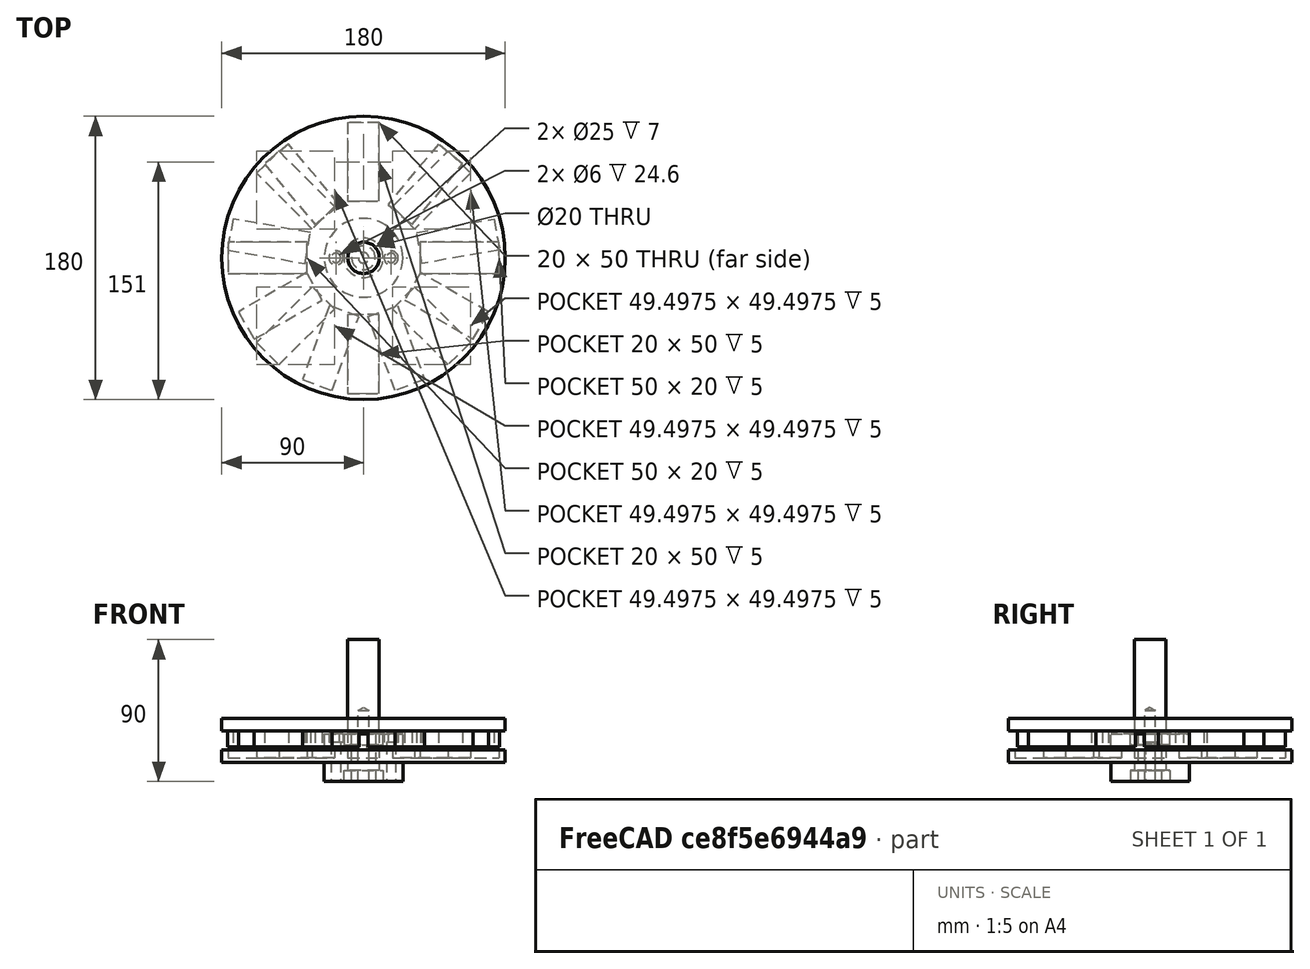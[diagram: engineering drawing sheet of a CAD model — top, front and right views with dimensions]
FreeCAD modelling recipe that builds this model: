
FCSTD DOCUMENT  (FreeCAD 0.20R29410 (Git))
Label: windTurbine
License: All rights reserved
LicenseURL: http://en.wikipedia.org/wiki/All_rights_reserved
objects: Sketcher::SketchObject×18, PartDesign::Pocket×10, PartDesign::Pad×6, TechDraw::DrawViewDimension×4, PartDesign::Hole×3, PartDesign::Body×3, PartDesign::Plane×1, TechDraw::DrawSVGTemplate×1, TechDraw::DrawViewPart×1, TechDraw::DrawViewSection×1, TechDraw::DrawViewSymbol×1, TechDraw::DrawPage×1
note: 60 computed .brp shape members not serialized (recipe doc carries the construction recipe); baked Part::Feature solids carry a one-line shape summary decoded from their .brp

FEATURE [Sketcher::SketchObject] Sketch  label="RotorDisc"
  FullyConstrained = true
  sketch-geometry (1):
    g0: Circle CenterX=0 CenterY=0 CenterZ=0 NormalX=0 NormalY=0 NormalZ=1 AngleXU=0 Radius=90
  constraints (2):
    c: Coincident(g0,g-1)
    c: Diameter(g0) = 180
FEATURE [Sketcher::SketchObject] Sketch001  label="Mag1"
  FullyConstrained = true
  MapMode = 5
  Support = -> [XY_Plane001]
  sketch-geometry (4):
    g0: LineSegment StartX=-10 StartY=86 StartZ=0 EndX=10 EndY=86 EndZ=0
    g1: LineSegment StartX=10 StartY=86 StartZ=0 EndX=10 EndY=36 EndZ=0
    g2: LineSegment StartX=10 StartY=36 StartZ=0 EndX=-10 EndY=36 EndZ=0
    g3: LineSegment StartX=-10 StartY=36 StartZ=0 EndX=-10 EndY=86 EndZ=0
  constraints (11):
    c: Coincident(g0,g1)
    c: Coincident(g1,g2)
    c: Coincident(g2,g3)
    c: Coincident(g3,g0)
    c: Horizontal(g2)
    c: Vertical(g1)
    c: Vertical(g3)
    c: Symmetric(g0,g0,g-2)
    c: DistanceY(g1,g1) = 50
    c: DistanceY(g-1,g1) = 36
    c: DistanceX(g0,g0) = 20
FEATURE [Sketcher::SketchObject] Sketch002  label="Mag2"
  FullyConstrained = true
  MapMode = 5
  Support = -> [XY_Plane001]
  sketch-geometry (4):
    g0: LineSegment StartX=-10 StartY=-36 StartZ=0 EndX=10 EndY=-36 EndZ=0
    g1: LineSegment StartX=10 StartY=-36 StartZ=0 EndX=10 EndY=-86 EndZ=0
    g2: LineSegment StartX=10 StartY=-86 StartZ=0 EndX=-10 EndY=-86 EndZ=0
    g3: LineSegment StartX=-10 StartY=-86 StartZ=0 EndX=-10 EndY=-36 EndZ=0
  constraints (12):
    c: Coincident(g0,g1)
    c: Coincident(g1,g2)
    c: Coincident(g2,g3)
    c: Coincident(g3,g0)
    c: Horizontal(g2)
    c: DistanceX(g0,g0) = 20
    c: DistanceY(g1,g0) = 50
    c: Angle(g3,g2,g2) = 1.5708
    c: Angle(g2,g1,g1) = 1.5708
    c: Angle(g0,g3,g0) = 1.5708
    c: DistanceX(g-1,g0) = 10
    c: DistanceY(g0,g-1) = 36
FEATURE [Sketcher::SketchObject] Sketch003  label="Mag3"
  FullyConstrained = true
  MapMode = 5
  Support = -> [XY_Plane001]
  sketch-geometry (4):
    g0: LineSegment StartX=36 StartY=10 StartZ=0 EndX=86 EndY=10 EndZ=0
    g1: LineSegment StartX=86 StartY=10 StartZ=0 EndX=86 EndY=-10 EndZ=0
    g2: LineSegment StartX=86 StartY=-10 StartZ=0 EndX=36 EndY=-10 EndZ=0
    g3: LineSegment StartX=36 StartY=-10 StartZ=0 EndX=36 EndY=10 EndZ=0
  constraints (11):
    c: Coincident(g0,g1)
    c: Coincident(g1,g2)
    c: Coincident(g2,g3)
    c: Coincident(g3,g0)
    c: Horizontal(g0)
    c: Horizontal(g2)
    c: Vertical(g1)
    c: DistanceX(g0,g0) = 50
    c: Symmetric(g2,g0,g-1)
    c: DistanceY(g3,g3) = 20
    c: DistanceX(g-1,g2) = 36
FEATURE [Sketcher::SketchObject] Sketch004  label="Mag4"
  FullyConstrained = true
  MapMode = 5
  Support = -> [XY_Plane001]
  sketch-geometry (4):
    g0: LineSegment StartX=-86 StartY=10 StartZ=0 EndX=-36 EndY=10 EndZ=0
    g1: LineSegment StartX=-36 StartY=10 StartZ=0 EndX=-36 EndY=-10 EndZ=0
    g2: LineSegment StartX=-36 StartY=-10 StartZ=0 EndX=-86 EndY=-10 EndZ=0
    g3: LineSegment StartX=-86 StartY=-10 StartZ=0 EndX=-86 EndY=10 EndZ=0
  constraints (12):
    c: Coincident(g0,g1)
    c: Coincident(g1,g2)
    c: Coincident(g2,g3)
    c: Coincident(g3,g0)
    c: DistanceY(g1,g0) = 20
    c: DistanceX(g0,g0) = 50
    c: Equal(g0,g2)
    c: Equal(g3,g1)
    c: Perpendicular(g3,g0)
    c: DistanceX(g0,g-1) = 36
    c: Perpendicular(g-2,g2)
    c: DistanceY(g-1,g0) = 10
FEATURE [Sketcher::SketchObject] Sketch005  label="Mag5"
  FullyConstrained = true
  MapMode = 5
  Support = -> [XY_Plane001]
  sketch-geometry (5):
    g0: LineSegment StartX=-63.6215 StartY=63.6215 StartZ=0 EndX=0 EndY=0 EndZ=0
    g1: LineSegment StartX=-67.8823 StartY=53.7401 StartZ=0 EndX=-32.5269 EndY=18.3848 EndZ=0
    g2: LineSegment StartX=-32.5269 StartY=18.3848 StartZ=0 EndX=-18.3848 EndY=32.5269 EndZ=0
    g3: LineSegment StartX=-18.3848 StartY=32.5269 StartZ=0 EndX=-53.7401 EndY=67.8823 EndZ=0
    g4: LineSegment StartX=-53.7401 StartY=67.8823 StartZ=0 EndX=-67.8823 EndY=53.7401 EndZ=0
  constraints (15):
    c: Coincident(g0,g-1)
    c: DistanceX(g0) = -63.6215
    c: Coincident(g1,g2)
    c: Coincident(g2,g3)
    c: Coincident(g3,g4)
    c: Coincident(g4,g1)
    c: Distance(g3,g0) = 10
    c: Distance(g2,g0) = 10
    c: Distance(g1,g0) = 10
    c: Distance(g1,g0) = 10
    c: Distance(g2,g3) = 50
    c: Distance(g1,g1) = 50
    c: Perpendicular(g1,g4)
    c: Distance(g0,g2) = 36
    c: Angle(g-1,g0) = 2.35619
FEATURE [Sketcher::SketchObject] Sketch006  label="Mag6"
  FullyConstrained = true
  MapMode = 5
  Support = -> [XY_Plane001]
  sketch-geometry (5):
    g0: LineSegment StartX=0 StartY=0 StartZ=0 EndX=70.7107 EndY=70.7107 EndZ=0
    g1: LineSegment StartX=18.3848 StartY=32.5269 StartZ=0 EndX=32.5269 EndY=18.3848 EndZ=0
    g2: LineSegment StartX=32.5269 StartY=18.3848 StartZ=0 EndX=67.8823 EndY=53.7401 EndZ=0
    g3: LineSegment StartX=67.8823 StartY=53.7401 StartZ=0 EndX=53.7401 EndY=67.8823 EndZ=0
    g4: LineSegment StartX=53.7401 StartY=67.8823 StartZ=0 EndX=18.3848 EndY=32.5269 EndZ=0
  constraints (15):
    c: Coincident(g0,g-1)
    c: Angle(g-1,g0) = 0.785398
    c: Coincident(g1,g2)
    c: Coincident(g2,g3)
    c: Coincident(g3,g4)
    c: Coincident(g4,g1)
    c: Distance(g1,g1) = 20
    c: Distance(g3,g2) = 20
    c: Distance(g2,g1) = 50
    c: Distance(g1,g3) = 50
    c: Distance(g0,g1) = 36
    c: Parallel(g4,g0)
    c: Perpendicular(g3,g4)
    c: Distance(g1,g0) = 10
    c: Distance(g0) = 100
FEATURE [Sketcher::SketchObject] Sketch007  label="Mag7"
  FullyConstrained = true
  MapMode = 5
  Support = -> [XY_Plane001]
  sketch-geometry (5):
    g0: LineSegment StartX=0 StartY=0 StartZ=0 EndX=-93.0623 EndY=-93.0623 EndZ=0
    g1: LineSegment StartX=-67.8823 StartY=-53.7401 StartZ=0 EndX=-53.7401 EndY=-67.8823 EndZ=0
    g2: LineSegment StartX=-53.7401 StartY=-67.8823 StartZ=0 EndX=-18.3848 EndY=-32.5269 EndZ=0
    g3: LineSegment StartX=-18.3848 StartY=-32.5269 StartZ=0 EndX=-32.5269 EndY=-18.3848 EndZ=0
    g4: LineSegment StartX=-32.5269 StartY=-18.3848 StartZ=0 EndX=-67.8823 EndY=-53.7401 EndZ=0
  constraints (15):
    c: Coincident(g0,g-1)
    c: Angle(g0,g-1) = 2.35619
    c: Distance(g0) = 131.61
    c: Coincident(g1,g2)
    c: Coincident(g2,g3)
    c: Coincident(g3,g4)
    c: Coincident(g4,g1)
    c: Distance(g4) = 50
    c: Distance(g2) = 50
    c: Distance(g3) = 20
    c: Distance(g1) = 20
    c: Perpendicular(g4,g1)
    c: Distance(g3,g0) = 10
    c: Distance(g0,g3) = 36
    c: Parallel(g0,g4)
FEATURE [Sketcher::SketchObject] Sketch008  label="Mag8"
  FullyConstrained = true
  MapMode = 5
  Support = -> [XY_Plane001]
  sketch-geometry (5):
    g0: LineSegment StartX=0 StartY=0 StartZ=0 EndX=70.7107 EndY=-70.7107 EndZ=0
    g1: LineSegment StartX=18.3848 StartY=-32.5269 StartZ=0 EndX=32.5269 EndY=-18.3848 EndZ=0
    g2: LineSegment StartX=32.5269 StartY=-18.3848 StartZ=0 EndX=67.8823 EndY=-53.7401 EndZ=0
    g3: LineSegment StartX=67.8823 StartY=-53.7401 StartZ=0 EndX=53.7401 EndY=-67.8823 EndZ=0
    g4: LineSegment StartX=53.7401 StartY=-67.8823 StartZ=0 EndX=18.3848 EndY=-32.5269 EndZ=0
  constraints (15):
    c: Coincident(g0,g-1)
    c: Angle(g0,g-1) = 0.785398
    c: Distance(g0) = 100
    c: Coincident(g1,g2)
    c: Coincident(g2,g3)
    c: Coincident(g3,g4)
    c: Coincident(g4,g1)
    c: Parallel(g4,g0)
    c: Perpendicular(g2,g3)
    c: Distance(g1) = 20
    c: Distance(g3) = 20
    c: Distance(g2) = 50
    c: Distance(g4) = 50
    c: Distance(g1,g0) = 10
    c: Distance(g0,g1) = 36
FEATURE [Sketcher::SketchObject] Sketch009  label="BearingSeatAndBoss"
  FullyConstrained = true
  MapMode = 5
  Support = -> [XY_Plane001]
  sketch-geometry (4):
    g0: Circle CenterX=0 CenterY=0 CenterZ=0 NormalX=0 NormalY=0 NormalZ=1 AngleXU=0 Radius=25
    g1: Circle CenterX=0 CenterY=0 CenterZ=0 NormalX=0 NormalY=0 NormalZ=1 AngleXU=0 Radius=17.5
    g2: GeomPoint X=-17.5 Y=0 Z=0
    g3: GeomPoint X=17.5 Y=0 Z=0
  constraints (8):
    c: Coincident(g0,g-1)
    c: Diameter(g0) = 50
    c: Coincident(g1,g0)
    c: Diameter(g1) = 35
    c: PointOnObject(g2,g1)
    c: PointOnObject(g3,g1)
    c: DistanceY(g2) = 0
    c: DistanceY(g3) = 0
FEATURE [PartDesign::Pad] Pad
  Direction = (0,0,1)
  Length = 8
  Length2 = 10
  Profile = -> Sketch
  ReferenceAxis = -> Sketch [N_Axis]
  Refine = true
  Type = 0
FEATURE [PartDesign::Pocket] Pocket
  BaseFeature = -> Pad
  Direction = (0,0,-1)
  Length = 5
  Length2 = 5
  Profile = -> Sketch001
  ReferenceAxis = -> Sketch001 [N_Axis]
  Refine = true
  Reversed = true
  Type = 0
FEATURE [PartDesign::Pocket] Pocket001
  BaseFeature = -> Pocket
  Direction = (0,0,-1)
  Length = 5
  Length2 = 5
  Profile = -> Sketch002
  ReferenceAxis = -> Sketch002 [N_Axis]
  Refine = true
  Reversed = true
  Type = 0
FEATURE [PartDesign::Pocket] Pocket002
  BaseFeature = -> Pocket001
  Direction = (0,0,-1)
  Length = 5
  Length2 = 5
  Profile = -> Sketch003
  ReferenceAxis = -> Sketch003 [N_Axis]
  Refine = true
  Reversed = true
  Type = 0
FEATURE [PartDesign::Pocket] Pocket003
  BaseFeature = -> Pocket002
  Direction = (0,0,-1)
  Length = 5
  Length2 = 5
  Profile = -> Sketch004
  ReferenceAxis = -> Sketch004 [N_Axis]
  Refine = true
  Reversed = true
  Type = 0
FEATURE [PartDesign::Pocket] Pocket004
  BaseFeature = -> Pocket003
  Direction = (0,0,-1)
  Length = 5
  Length2 = 5
  Profile = -> Sketch005
  ReferenceAxis = -> Sketch005 [N_Axis]
  Refine = true
  Reversed = true
  Type = 0
FEATURE [PartDesign::Pocket] Pocket005
  BaseFeature = -> Pocket004
  Direction = (0,0,-1)
  Length = 5
  Length2 = 5
  Profile = -> Sketch006
  ReferenceAxis = -> Sketch006 [N_Axis]
  Refine = true
  Reversed = true
  Type = 0
FEATURE [PartDesign::Pocket] Pocket006
  BaseFeature = -> Pocket005
  Direction = (0,0,-1)
  Length = 5
  Length2 = 5
  Profile = -> Sketch007
  ReferenceAxis = -> Sketch007 [N_Axis]
  Refine = true
  Reversed = true
  Type = 0
FEATURE [PartDesign::Pocket] Pocket007
  BaseFeature = -> Pocket006
  Direction = (0,0,-1)
  Length = 5
  Length2 = 5
  Profile = -> Sketch008
  ReferenceAxis = -> Sketch008 [N_Axis]
  Refine = true
  Reversed = true
  Type = 0
FEATURE [PartDesign::Pad] Pad001
  BaseFeature = -> Pocket007
  Direction = (0,0,1)
  Length = 20
  Length2 = 10
  Profile = -> Sketch009
  ReferenceAxis = -> Sketch009 [N_Axis]
  Refine = true
  Type = 4
FEATURE [Sketcher::SketchObject] Sketch010
  FullyConstrained = true
  MapMode = 5
  Placement = pos=(0,0,-10) rot=(1,0,0;3.14159rad)
  Support = -> [Pad001]
  sketch-geometry (1):
    g0: Circle CenterX=0 CenterY=0 CenterZ=0 NormalX=0 NormalY=0 NormalZ=1 AngleXU=0 Radius=10
  constraints (2):
    c: Coincident(g0,g-1)
    c: Diameter(g0) = 20
FEATURE [PartDesign::Hole] Hole
  BaseFeature = -> Pad001
  CustomThreadClearance = 0
  Depth = 517.767
  DepthType = 1
  Diameter = 20
  DrillForDepth = false
  DrillPoint = 1
  DrillPointAngle = 118
  HoleCutCountersinkAngle = 90
  HoleCutCustomValues = false
  HoleCutDepth = 0
  HoleCutDiameter = 6.1
  HoleCutType = 0
  ModelThread = false
  Profile = -> Sketch010
  Refine = true
  Tapered = false
  TaperedAngle = 90
  ThreadClass = 0
  ThreadDepth = 517.767
  ThreadDepthType = 0
  ThreadDirection = 0
  ThreadFit = 0
  ThreadSize = 0
  ThreadType = 0
  Threaded = false
  UseCustomThreadClearance = false
FEATURE [Sketcher::SketchObject] Sketch011
  FullyConstrained = true
  MapMode = 5
  Placement = pos=(0,0,-10) rot=(1,0,0;3.14159rad)
  Support = -> [Hole]
  sketch-geometry (1):
    g0: Circle CenterX=0 CenterY=0 CenterZ=0 NormalX=0 NormalY=0 NormalZ=1 AngleXU=0 Radius=12.5
  constraints (2):
    c: Coincident(g0,g-1)
    c: Diameter(g0) = 25
FEATURE [PartDesign::Pocket] Pocket008
  BaseFeature = -> Hole
  Direction = (0,0,1)
  Length = 7
  Length2 = 5
  Profile = -> Sketch011
  ReferenceAxis = -> Sketch011 [N_Axis]
  Refine = true
  Type = 0
FEATURE [Sketcher::SketchObject] Sketch012
  FullyConstrained = true
  MapMode = 5
  Placement = pos=(0,0,20) rot=(0,0,1;0rad)
  Support = -> [Pocket008]
  sketch-geometry (1):
    g0: Circle CenterX=0 CenterY=0 CenterZ=0 NormalX=0 NormalY=0 NormalZ=1 AngleXU=0 Radius=12.5
  constraints (2):
    c: Coincident(g0,g-1)
    c: Diameter(g0) = 25
FEATURE [PartDesign::Pocket] Pocket009
  BaseFeature = -> Pocket008
  Direction = (0,0,-1)
  Length = 7
  Length2 = 5
  Profile = -> Sketch012
  ReferenceAxis = -> Sketch012 [N_Axis]
  Refine = true
  Type = 0
FEATURE [Sketcher::SketchObject] Sketch013
  FullyConstrained = true
  MapMode = 5
  Placement = pos=(0,0,-10) rot=(1,0,0;3.14159rad)
  Support = -> [Pocket009]
  sketch-geometry (5):
    g0: Circle CenterX=0 CenterY=0 CenterZ=0 NormalX=0 NormalY=0 NormalZ=1 AngleXU=0 Radius=17.5
    g1: GeomPoint X=-17.5 Y=0 Z=0
    g2: GeomPoint X=17.5 Y=0 Z=0
    g3: Circle CenterX=17.5 CenterY=0 CenterZ=0 NormalX=0 NormalY=0 NormalZ=1 AngleXU=0 Radius=3
    g4: Circle CenterX=-17.5 CenterY=0 CenterZ=0 NormalX=0 NormalY=0 NormalZ=1 AngleXU=0 Radius=3
  constraints (10):
    c: Coincident(g0,g-1)
    c: PointOnObject(g1,g0)
    c: PointOnObject(g2,g0)
    c: Diameter(g0) = 35
    c: DistanceY(g1) = 0
    c: DistanceY(g2) = 0
    c: Coincident(g3,g2)
    c: Coincident(g4,g1)
    c: Diameter(g3) = 6
    c: Diameter(g4) = 6
FEATURE [PartDesign::Hole] Hole001
  BaseFeature = -> Pocket009
  CustomThreadClearance = 0
  Depth = 517.767
  DepthType = 1
  Diameter = 6
  DrillForDepth = false
  DrillPoint = 1
  DrillPointAngle = 118
  HoleCutCountersinkAngle = 90
  HoleCutCustomValues = false
  HoleCutDepth = 5.4
  HoleCutDiameter = 9
  HoleCutType = 1
  ModelThread = false
  Profile = -> Sketch013
  Refine = true
  Tapered = false
  TaperedAngle = 90
  ThreadClass = 0
  ThreadDepth = 517.767
  ThreadDepthType = 0
  ThreadDirection = 0
  ThreadFit = 0
  ThreadSize = 0
  ThreadType = 0
  Threaded = false
  UseCustomThreadClearance = false
FEATURE [PartDesign::Body] Body  label="RotorBody"
  Group = -> [Sketch,Sketch001,Sketch002,Sketch003,Sketch004,Sketch005,Sketch006,Sketch007,Sketch008,Sketch009,Pad,Pocket,Pocket001,Pocket002,Pocket003,Pocket004,Pocket005,Pocket006,Pocket007,Pad001,Sketch010,Hole,Sketch011,Pocket008,Sketch012,Pocket009,Sketch013,Hole001]
  Origin = -> Origin001
  Placement = pos=(-1e-15,0,10) rot=(0,1,0;3.14159rad)
  Tip = -> Hole001
FEATURE [Sketcher::SketchObject] Sketch014
  FullyConstrained = true
  MapMode = 5
  Placement = pos=(0,0,20) rot=(0,0,1;0rad)
  sketch-geometry (1):
    g0: Circle CenterX=0 CenterY=0 CenterZ=0 NormalX=0 NormalY=0 NormalZ=1 AngleXU=0 Radius=10
  constraints (2):
    c: Coincident(g0,g-1)
    c: Diameter(g0) = 20
FEATURE [PartDesign::Pad] Pad002
  Direction = (0,0,1)
  Length = 60
  Length2 = 10
  Placement = pos=(0,0,20) rot=(0,0,1;0rad)
  Profile = -> Sketch014
  ReferenceAxis = -> Sketch014 [N_Axis]
  Refine = true
  Type = 0
FEATURE [Sketcher::SketchObject] Sketch015
  FullyConstrained = true
  MapMode = 5
  Placement = pos=(0,0,20) rot=(1,0,0;3.14159rad)
  Support = -> [Pad002]
  sketch-geometry (1):
    g0: Circle CenterX=0 CenterY=0 CenterZ=0 NormalX=0 NormalY=0 NormalZ=1 AngleXU=0 Radius=7.5
  constraints (2):
    c: Coincident(g0,g-1)
    c: Diameter(g0) = 15
FEATURE [PartDesign::Pad] Pad003
  BaseFeature = -> Pad002
  Direction = (0,0,-1)
  Length = 30
  Length2 = 10
  Placement = pos=(0,0,20) rot=(0,0,1;0rad)
  Profile = -> Sketch015
  ReferenceAxis = -> Sketch015 [N_Axis]
  Refine = true
  Type = 0
FEATURE [PartDesign::Hole] Hole002
  BaseFeature = -> Pad003
  CustomThreadClearance = 0
  Depth = 45
  DepthType = 0
  Diameter = 6.8
  DrillForDepth = false
  DrillPoint = 1
  DrillPointAngle = 118
  HoleCutCountersinkAngle = 90
  HoleCutCustomValues = false
  HoleCutDepth = 0
  HoleCutDiameter = 6.1
  HoleCutType = 0
  ModelThread = false
  Placement = pos=(0,0,20) rot=(0,0,1;0rad)
  Profile = -> Pad003 [Face5]
  Refine = true
  Tapered = false
  TaperedAngle = 90
  ThreadClass = 0
  ThreadDepth = 45
  ThreadDepthType = 0
  ThreadDirection = 0
  ThreadFit = 0
  ThreadSize = 16
  ThreadType = 1
  Threaded = true
  UseCustomThreadClearance = false
FEATURE [PartDesign::Body] Body001  label="Shaft"
  Group = -> [Sketch014,Pad002,Sketch015,Pad003,Hole002]
  Origin = -> Origin
  Tip = -> Hole002
FEATURE [PartDesign::Plane] DatumPlane
  AttachmentOffset = pos=(0,0,21) rot=(0,0,1;0rad)
  Length = 216
  MapMode = 5
  Placement = pos=(0,0,21) rot=(0,0,1;0rad)
  ResizeMode = 0
  Support = -> [XY_Plane001]
  Width = 216
FEATURE [Sketcher::SketchObject] Sketch016
  FullyConstrained = true
  MapMode = 5
  Placement = pos=(0,0,21) rot=(0,0,1;0rad)
  Support = -> [DatumPlane]
  sketch-geometry (2):
    g0: Circle CenterX=0 CenterY=0 CenterZ=0 NormalX=0 NormalY=0 NormalZ=1 AngleXU=0 Radius=90
    g1: Circle CenterX=0 CenterY=0 CenterZ=0 NormalX=0 NormalY=0 NormalZ=1 AngleXU=0 Radius=10
  constraints (4):
    c: Coincident(g0,g-1)
    c: Diameter(g0) = 180
    c: Coincident(g1,g0)
    c: Diameter(g1) = 20
FEATURE [PartDesign::Pad] Pad004
  Direction = (0,0,1)
  Length = 8
  Length2 = 10
  Placement = pos=(0,0,21) rot=(0,0,1;0rad)
  Profile = -> Sketch016
  ReferenceAxis = -> Sketch016 [N_Axis]
  Refine = true
  Type = 0
FEATURE [Sketcher::SketchObject] Sketch017
  FullyConstrained = true
  MapMode = 5
  Placement = pos=(0,0,21) rot=(0,0,1;0rad)
  Support = -> [DatumPlane]
  sketch-geometry (50):
    g0: LineSegment StartX=0 StartY=0 StartZ=0 EndX=0 EndY=10 EndZ=0
    g1: LineSegment StartX=0 StartY=0 StartZ=0 EndX=6.42788 EndY=7.66044 EndZ=0
    g2: LineSegment StartX=0 StartY=0 StartZ=0 EndX=9.84808 EndY=1.73648 EndZ=0
    g3: LineSegment StartX=0 StartY=0 StartZ=0 EndX=8.66025 EndY=-5 EndZ=0
    g4: LineSegment StartX=0 StartY=0 StartZ=0 EndX=3.4202 EndY=-9.39693 EndZ=0
    g5: LineSegment StartX=0 StartY=0 StartZ=0 EndX=-3.4202 EndY=-9.39693 EndZ=0
    g6: LineSegment StartX=0 StartY=0 StartZ=0 EndX=-8.66025 EndY=-5 EndZ=0
    g7: LineSegment StartX=0 StartY=0 StartZ=0 EndX=-9.84808 EndY=1.73648 EndZ=0
    g8: LineSegment StartX=0 StartY=0 StartZ=0 EndX=-6.42788 EndY=7.66044 EndZ=0
    g9: LineSegment StartX=-10 StartY=86 StartZ=0 EndX=-10 EndY=36 EndZ=0
    g10: LineSegment StartX=-10 StartY=36 StartZ=0 EndX=10 EndY=36 EndZ=0
    g11: LineSegment StartX=10 StartY=36 StartZ=0 EndX=10 EndY=86 EndZ=0
    g12: LineSegment StartX=10 StartY=86 StartZ=0 EndX=-10 EndY=86 EndZ=0
    g13: LineSegment StartX=15.4799 StartY=34.0055 StartZ=0 EndX=30.8008 EndY=21.1497 EndZ=0
    g14: LineSegment StartX=30.8008 StartY=21.1497 StartZ=0 EndX=62.9402 EndY=59.4519 EndZ=0
    g15: LineSegment StartX=62.9402 StartY=59.4519 StartZ=0 EndX=47.6193 EndY=72.3077 EndZ=0
    g16: LineSegment StartX=47.6193 StartY=72.3077 StartZ=0 EndX=15.4799 EndY=34.0055 EndZ=0
    g17: LineSegment StartX=37.1896 StartY=-3.59674 StartZ=0 EndX=33.7166 EndY=16.0994 EndZ=0
    g18: LineSegment StartX=33.7166 StartY=16.0994 StartZ=0 EndX=82.957 EndY=24.7818 EndZ=0
    g19: LineSegment StartX=82.957 StartY=24.7818 StartZ=0 EndX=86.4299 EndY=5.08567 EndZ=0
    g20: LineSegment StartX=86.4299 StartY=5.08567 StartZ=0 EndX=37.1896 EndY=-3.59674 EndZ=0
    g21: LineSegment StartX=36.1769 StartY=-9.33975 StartZ=0 EndX=26.1769 EndY=-26.6603 EndZ=0
    g22: LineSegment StartX=26.1769 StartY=-26.6603 StartZ=0 EndX=69.4782 EndY=-51.6603 EndZ=0
    g23: LineSegment StartX=69.4782 StartY=-51.6603 StartZ=0 EndX=79.4782 EndY=-34.3397 EndZ=0
    g24: LineSegment StartX=79.4782 StartY=-34.3397 StartZ=0 EndX=36.1769 EndY=-9.33975 EndZ=0
    g25: LineSegment StartX=2.9158 StartY=-37.2492 StartZ=0 EndX=21.7096 EndY=-30.4087 EndZ=0
    g26: LineSegment StartX=21.7096 StartY=-30.4087 StartZ=0 EndX=38.8107 EndY=-77.3933 EndZ=0
    g27: LineSegment StartX=38.8107 StartY=-77.3933 StartZ=0 EndX=20.0168 EndY=-84.2338 EndZ=0
    g28: LineSegment StartX=20.0168 StartY=-84.2338 StartZ=0 EndX=2.9158 EndY=-37.2492 EndZ=0
    g29: LineSegment StartX=-20.0168 StartY=-84.2338 StartZ=0 EndX=-2.9158 EndY=-37.2491 EndZ=0
    g30: LineSegment StartX=-2.9158 StartY=-37.2491 StartZ=0 EndX=-21.7097 EndY=-30.4087 EndZ=0
    g31: LineSegment StartX=-21.7097 StartY=-30.4087 StartZ=0 EndX=-38.8107 EndY=-77.3934 EndZ=0
    g32: LineSegment StartX=-38.8107 StartY=-77.3934 StartZ=0 EndX=-20.0168 EndY=-84.2338 EndZ=0
    g33: LineSegment StartX=-79.4782 StartY=-34.3397 StartZ=0 EndX=-69.4782 EndY=-51.6603 EndZ=0
    g34: LineSegment StartX=-69.4782 StartY=-51.6603 StartZ=0 EndX=-26.1769 EndY=-26.6603 EndZ=0
    g35: LineSegment StartX=-26.1769 StartY=-26.6603 StartZ=0 EndX=-36.1769 EndY=-9.33975 EndZ=0
    g36: LineSegment StartX=-36.1769 StartY=-9.33975 StartZ=0 EndX=-79.4782 EndY=-34.3397 EndZ=0
    g37: LineSegment StartX=-82.957 StartY=24.7818 StartZ=0 EndX=-86.4299 EndY=5.08567 EndZ=0
    g38: LineSegment StartX=-86.4299 StartY=5.08567 StartZ=0 EndX=-37.1896 EndY=-3.59674 EndZ=0
    g39: LineSegment StartX=-37.1896 StartY=-3.59674 StartZ=0 EndX=-33.7166 EndY=16.0994 EndZ=0
    g40: LineSegment StartX=-33.7166 StartY=16.0994 StartZ=0 EndX=-82.957 EndY=24.7818 EndZ=0
    g41: LineSegment StartX=-47.6193 StartY=72.3077 StartZ=0 EndX=-62.9402 EndY=59.4519 EndZ=0
    g42: LineSegment StartX=-62.9402 StartY=59.4519 StartZ=0 EndX=-30.8008 EndY=21.1497 EndZ=0
    g43: LineSegment StartX=-30.8008 StartY=21.1497 StartZ=0 EndX=-15.4799 EndY=34.0055 EndZ=0
    g44: LineSegment StartX=-15.4799 StartY=34.0055 StartZ=0 EndX=-47.6193 EndY=72.3077 EndZ=0
    g45: GeomPoint X=-12.3127 Y=-33.8289 Z=0
    g46: GeomPoint X=-31.1769 Y=-18 Z=0
    g47: GeomPoint X=12.3127 Y=-33.8289 Z=0
    g48: GeomPoint X=-35.4531 Y=6.25133 Z=0
    g49: GeomPoint X=-23.1404 Y=27.5776 Z=0
  constraints (145):
    c: Coincident(g0,g-1)
    c: PointOnObject(g0,g-2)
    c: Coincident(g1,g0)
    c: Angle(g1,g0) = 0.698132
    c: Coincident(g2,g0)
    c: Angle(g2,g1) = 0.698132
    c: Coincident(g3,g0)
    c: Angle(g3,g2) = 0.698132
    c: Coincident(g4,g0)
    c: Coincident(g5,g0)
    c: Coincident(g6,g0)
    c: Coincident(g7,g0)
    c: Coincident(g8,g0)
    c: Angle(g4,g3) = 0.698132
    c: Angle(g5,g4) = 0.698132
    c: Angle(g6,g5) = 0.698132
    c: Angle(g7,g6) = 0.698132
    c: Angle(g8,g7) = 0.698132
    c: Vertical(g9)
    c: Coincident(g9,g10)
    c: Coincident(g10,g11)
    c: Vertical(g11)
    c: Coincident(g11,g12)
    c: Coincident(g12,g9)
    c: Horizontal(g12)
    c: Coincident(g13,g14)
    c: Coincident(g14,g15)
    c: Coincident(g15,g16)
    c: Coincident(g16,g13)
    c: Coincident(g17,g18)
    c: Coincident(g18,g19)
    c: Coincident(g19,g20)
    c: Coincident(g20,g17)
    c: Coincident(g21,g22)
    c: Coincident(g22,g23)
    c: Coincident(g23,g24)
    c: Coincident(g24,g21)
    c: Coincident(g25,g26)
    c: Coincident(g26,g27)
    c: Coincident(g27,g28)
    c: Coincident(g28,g25)
    c: Coincident(g29,g30)
    c: Coincident(g30,g31)
    c: Coincident(g31,g32)
    c: Coincident(g32,g29)
    c: Coincident(g33,g34)
    c: Coincident(g34,g35)
    c: Coincident(g35,g36)
    c: Coincident(g36,g33)
    c: Coincident(g37,g38)
    c: Coincident(g38,g39)
    c: Coincident(g39,g40)
    c: Coincident(g40,g37)
    c: Coincident(g41,g42)
    c: Coincident(g42,g43)
    c: Coincident(g43,g44)
    c: Coincident(g44,g41)
    c: Parallel(g12,g10)
    c: Distance(g0,g10) = 36
    c: Distance(g9,g0) = 10
    c: Distance(g11,g0) = 10
    c: Parallel(g16,g14)
    c: Parallel(g13,g15)
    c: Distance(g13,g1) = 10
    c: Distance(g11,g10) = 50
    c: Distance(g15,g13) = 50
    c: Distance(g0,g13) = 36
    c: Distance(g15,g1) = 10
    c: Distance(g14,g1) = 10
    c: Perpendicular(g14,g13)
    c: Distance(g0,g17) = 36
    c: Parallel(g20,g2)
    c: Parallel(g18,g2)
    c: Distance(g17,g2) = 10
    c: Distance(g17,g2) = 10
    c: Parallel(g19,g17)
    c: Perpendicular(g19,g20)
    c: Distance(g19,g17) = 50
    c: Distance(g0,g21) = 36
    c: Parallel(g24,g22)
    c: Distance(g21,g22) = 50
    c: Distance(g21,g23) = 50
    c: Distance(g21,g3) = 10
    c: Distance(g21,g3) = 10
    c: Distance(g23,g3) = 10
    c: Perpendicular(g23,g22)
    c: Distance(g26) = 50
    c: Distance(g28) = 50
    c: Distance(g25) = 20
    c: Distance(g27) = 20
    c: Distance(g27,g4) = 10
    c: Distance(g26,g4) = 10
    c: Parallel(g28,g4)
    c: Parallel(g32,g30)
    c: Parallel(g31,g29)
    c: Distance(g31) = 50
    c: Perpendicular(g32,g29)
    c: Parallel(g29,g5)
    c: Distance(g30,g5) = 10
    c: Distance(g29,g5) = 10
    c: PointOnObject(g45,g30)
    c: PointOnObject(g45,g5)
    c: Distance(g45,g0) = 36
    c: Distance(g33,g6) = 10
    c: Distance(g34,g35) = 20
    c: Equal(g35,g33)
    c: Equal(g36,g34)
    c: Distance(g33,g35) = 50
    c: Distance(g34,g6) = 10
    c: PointOnObject(g46,g35)
    c: PointOnObject(g46,g6)
    c: Distance(g46,g0) = 36
    c: Perpendicular(g34,g33)
    c: PointOnObject(g47,g4)
    c: PointOnObject(g47,g25)
    c: Distance(g0,g47) = 36
    c: Distance(g38,g7) = 10
    c: Distance(g39,g7) = 10
    c: Distance(g37) = 20
    c: Distance(g37,g39) = 50
    c: Distance(g38) = 50
    c: Distance(g37,g7) = 10
    c: Perpendicular(g37,g40)
    c: PointOnObject(g48,g39)
    c: PointOnObject(g48,g7)
    c: Distance(g48,g0) = 36
    c: Distance(g42,g43) = 20
    c: Distance(g41,g8) = 10
    c: Distance(g42,g8) = 10
    c: Perpendicular(g42,g41)
    c: Perpendicular(g41,g44)
    c: Distance(g41,g43) = 50
    c: Distance(g42) = 50
    c: PointOnObject(g49,g43)
    c: PointOnObject(g49,g8)
    c: Distance(g49,g0) = 36
    c: Distance(g2) = 10
    c: Distance(g1) = 10
    c: Distance(g0) = 10
    c: Distance(g8) = 10
    c: Distance(g7) = 10
    c: Distance(g6) = 10
    c: Distance(g5) = 10
    c: Distance(g4) = 10
    c: Distance(g3) = 10
FEATURE [PartDesign::Pad] Pad005
  BaseFeature = -> Pad004
  Direction = (0,0,1)
  Length = 10
  Length2 = 10
  Placement = pos=(0,0,21) rot=(0,0,1;0rad)
  Profile = -> Sketch017
  ReferenceAxis = -> Sketch017 [N_Axis]
  Refine = true
  Reversed = true
  Type = 0
FEATURE [PartDesign::Body] Body002  label="Stator"
  Group = -> [DatumPlane,Sketch016,Pad004,Sketch017,Pad005]
  Origin = -> Origin002
  Placement = pos=(0,0,1) rot=(0,0,1;0rad)
  Tip = -> Pad005
FEATURE [TechDraw::DrawSVGTemplate] Template
  EditableTexts = APPROVER_NAME=Adrian Pilkington; AUTHOR_NAME=Adrian Pilkington; DATE=2022-9-30; DN=1; DOCUMENT_TYPE=Mechanical assembly drawing; OWNER_NAME=Adrian Pilkington; PM=Aluminium; PN=1; REVISION=REV A; RIGHTS=(R) DO NOT DUPLICATE THIS DRAWING TO THIRD PARTIES WITHOUT OWNER'S PERMISSION!; SCALE=1:1; SHEET=1 of 3; SIZE=A3; TITLELINE-1=Wind Turbine; TOLERANCE=0.01mm
  Height = 297
  Orientation = 1
  Width = 420
FEATURE [TechDraw::DrawViewPart] View001
  CoarseView = false
  Direction = (0,0,-1)
  Focus = 100
  HardHidden = false
  IsoCount = 0
  IsoHidden = false
  IsoVisible = false
  LockPosition = false
  Perspective = false
  Rotation = 0
  ScaleType = 0
  SeamHidden = false
  SeamVisible = true
  SmoothHidden = false
  SmoothVisible = true
  Source = -> [Body,Body001,Body002]
  X = 260.51
  XDirection = (0,-1,0)
  Y = 173.126
FEATURE [TechDraw::DrawViewSection] SectionView  label="Section  - "
  BaseView = -> View001
  CoarseView = false
  CutSurfaceDisplay = 2
  Direction = (0,-1,0)
  FileGeomPattern = C:/Program Files/FreeCAD 0.20/data/Mod/TechDraw/PAT/FCPAT.pat
  FileHatchPattern = C:/Program Files/FreeCAD 0.20/data/Mod/TechDraw/Patterns/simple.svg
  Focus = 100
  FuseBeforeCut = false
  HardHidden = false
  HatchScale = 1
  IsoCount = 0
  IsoHidden = false
  IsoVisible = false
  LockPosition = false
  NameGeomPattern = Diamond
  Perspective = false
  Rotation = 0
  ScaleType = 0
  SeamHidden = false
  SeamVisible = true
  SectionDirection = 1
  SectionNormal = (0,-1,0)
  SectionOrigin = (0,0,35)
  SmoothHidden = false
  SmoothVisible = true
  Source = -> [Body,Body001,Body002]
  X = 112.45
  XDirection = (0,0,1)
  Y = 173.438
FEATURE [TechDraw::DrawViewDimension] Dimension005
  AngleOverride = false
  Arbitrary = false
  ArbitraryTolerances = false
  EqualTolerance = true
  ExtensionAngle = 0
  FormatSpec = %.2w
  FormatSpecOverTolerance = %+.2w
  FormatSpecUnderTolerance = %+.2w
  Inverted = false
  LineAngle = 0
  LockPosition = false
  MeasureType = 1
  OverTolerance = 0
  References2D = -> [SectionView]
  Rotation = 0
  ScaleType = 0
  TheoreticalExact = false
  Type = 0
  UnderTolerance = 0
  X = -22.5
  Y = 5.9
FEATURE [TechDraw::DrawViewDimension] Dimension006
  AngleOverride = false
  Arbitrary = false
  ArbitraryTolerances = false
  EqualTolerance = true
  ExtensionAngle = 0
  FormatSpec = %.2w
  FormatSpecOverTolerance = %+.2w
  FormatSpecUnderTolerance = %+.2w
  Inverted = false
  LineAngle = 0
  LockPosition = false
  MeasureType = 1
  OverTolerance = 0
  References2D = -> [SectionView]
  Rotation = 0
  ScaleType = 0
  TheoreticalExact = false
  Type = 0
  UnderTolerance = 0
  X = -45
  Y = -15
FEATURE [TechDraw::DrawViewDimension] Dimension007
  AngleOverride = false
  Arbitrary = false
  ArbitraryTolerances = false
  EqualTolerance = true
  ExtensionAngle = 0
  FormatSpec = %.2w
  FormatSpecOverTolerance = %+.2w
  FormatSpecUnderTolerance = %+.2w
  Inverted = false
  LineAngle = 0
  LockPosition = false
  MeasureType = 1
  OverTolerance = 0
  References2D = -> [SectionView]
  Rotation = 0
  ScaleType = 0
  TheoreticalExact = false
  Type = 0
  UnderTolerance = 0
  X = -33
  Y = -55
FEATURE [TechDraw::DrawViewDimension] Dimension008
  AngleOverride = false
  Arbitrary = false
  ArbitraryTolerances = false
  EqualTolerance = true
  ExtensionAngle = 0
  FormatSpec = %.2w
  FormatSpecOverTolerance = %+.2w
  FormatSpecUnderTolerance = %+.2w
  Inverted = false
  LineAngle = 0
  LockPosition = false
  MeasureType = 1
  OverTolerance = 0
  References2D = -> [SectionView]
  Rotation = 0
  ScaleType = 0
  TheoreticalExact = false
  Type = 0
  UnderTolerance = 0
  X = -30
  Y = 63.5
FEATURE [TechDraw::DrawViewSymbol] ActiveView001
  LockPosition = false
  Rotation = 0
  ScaleType = 2
  Symbol = <blob: 2499843 chars omitted>
  X = 110.343
  Y = 28.6047
FEATURE [TechDraw::DrawPage] Page
  KeepUpdated = true
  NextBalloonIndex = 1
  ProjectionType = 0
  Template = -> Template
  Views = -> [View001,SectionView,Dimension005,Dimension006,Dimension007,Dimension008,ActiveView001]
